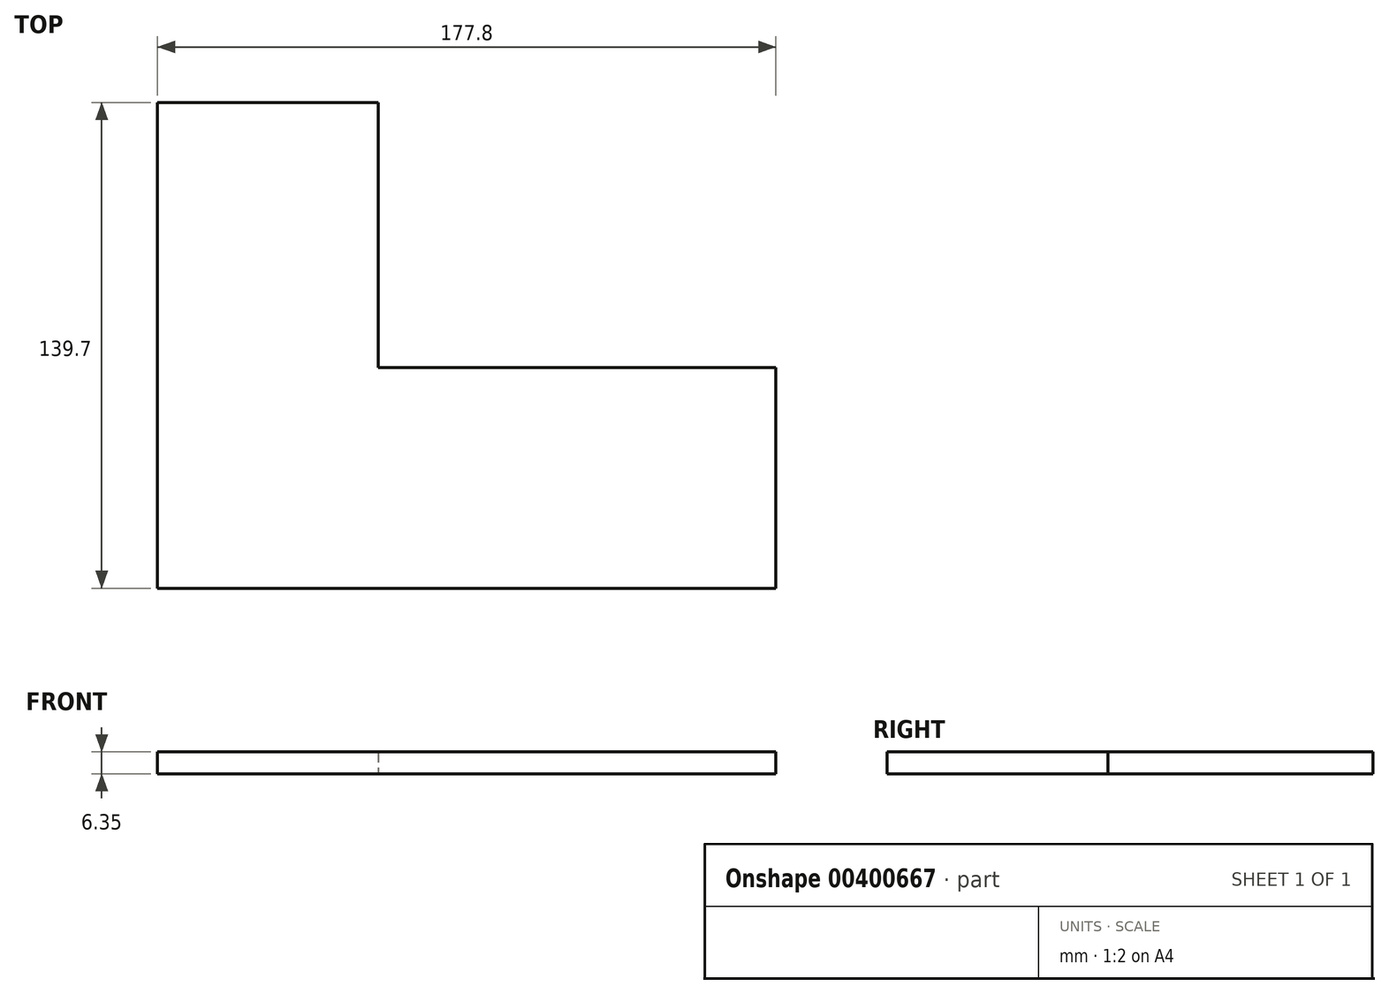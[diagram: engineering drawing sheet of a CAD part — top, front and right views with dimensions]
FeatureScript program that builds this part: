
annotation { "Feature Type Name" : "Feature", "Feature Type Description" : "" }
export const myFeature = defineFeature(function(context is Context, id is Id, definition is map)
    precondition{}
    {
        {
            var Q0;
            Q0=qCreatedBy(makeId("Top.planeOp"),FACE);
            var sketch = newSketch(context, id + "F0", { "sketchPlane" : qUnion([Q0])});
            skLineSegment(sketch, "E0", {"start": v(0, 0) * mm, "end": v(-177.8, 0) * mm});
            skLineSegment(sketch, "E1", {"start": v(-177.8, 0) * mm, "end": v(-177.8, 139.7) * mm});
            skLineSegment(sketch, "E2", {"start": v(-177.8, 139.7) * mm, "end": v(-114.3, 139.7) * mm});
            skLineSegment(sketch, "E3", {"start": v(0, 0) * mm, "end": v(0, 63.5) * mm});
            skLineSegment(sketch, "E4", {"start": v(-114.3, 139.7) * mm, "end": v(-114.3, 63.5) * mm});
            skLineSegment(sketch, "E5", {"start": v(-114.3, 63.5) * mm, "end": v(0, 63.5) * mm});
            skSolve(sketch);
        }
        {
            var Q0;
            Q0 = qSketchRegion(id + "F0", true);
            extrude(context, id + "F1", {"entities" : qUnion([Q0]), "depth" : 6.35 * mm});
        }
    });
